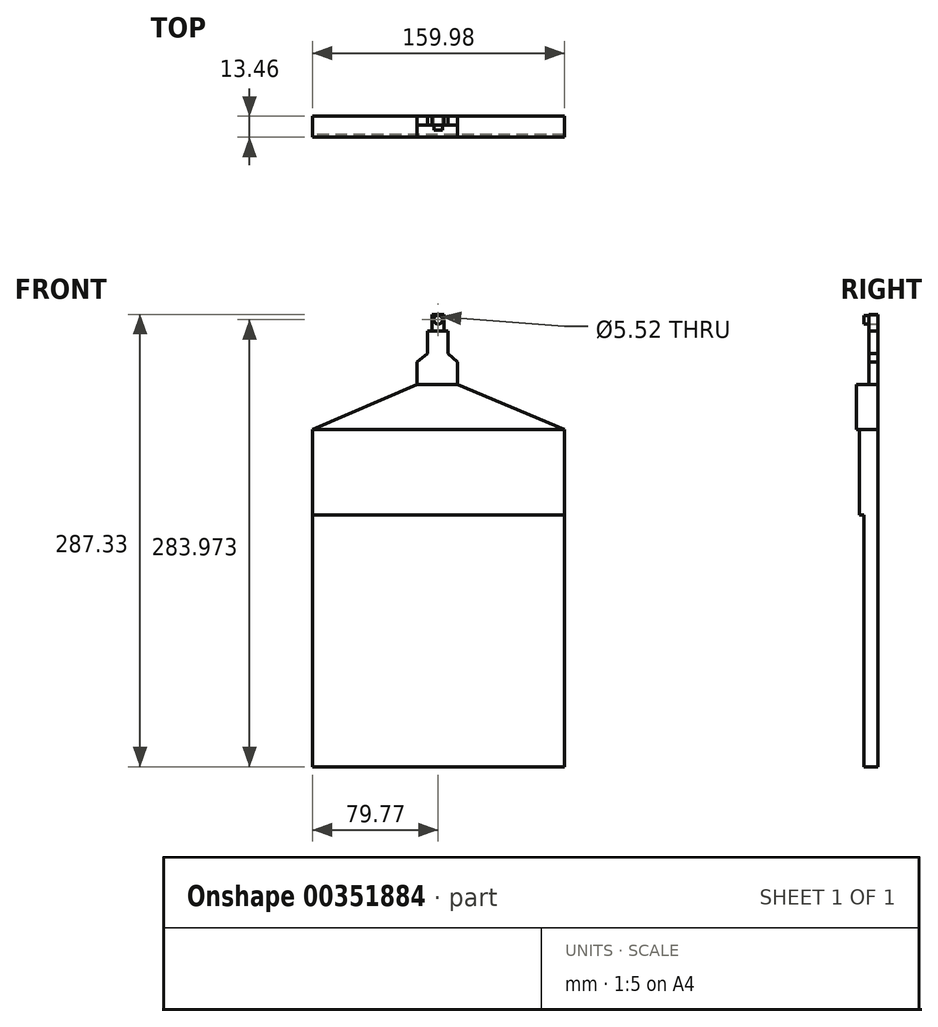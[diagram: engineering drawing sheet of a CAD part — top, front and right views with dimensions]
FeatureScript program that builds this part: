
annotation { "Feature Type Name" : "Feature", "Feature Type Description" : "" }
export const myFeature = defineFeature(function(context is Context, id is Id, definition is map)
    precondition{}
    {
        {
            var Q0;
            Q0=qCreatedBy(makeId("Front.planeOp"),FACE);
            var sketch = newSketch(context, id + "F0", { "sketchPlane" : qUnion([Q0])});
            skLineSegment(sketch, "E0", {"start": v(80.21, 80.05) * mm, "end": v(-79.77, 80.05) * mm});
            skLineSegment(sketch, "E1", {"start": v(-79.77, 80.05) * mm, "end": v(-79.77, 134.36) * mm});
            skLineSegment(sketch, "E2", {"start": v(80.21, 80.05) * mm, "end": v(80.21, 134.36) * mm});
            skLineSegment(sketch, "E3", {"start": v(-79.77, 134.36) * mm, "end": v(80.21, 134.36) * mm});
            skLineSegment(sketch, "E4", {"start": v(-79.77, 80.05) * mm, "end": v(-79.77, -79.93) * mm});
            skLineSegment(sketch, "E5", {"start": v(80.21, 80.05) * mm, "end": v(80.21, -79.93) * mm});
            skLineSegment(sketch, "E6", {"start": v(-79.77, -79.93) * mm, "end": v(80.21, -79.93) * mm});
            skLineSegment(sketch, "E7", {"start": v(-79.77, 134.36) * mm, "end": v(-13.44, 162.73) * mm});
            skLineSegment(sketch, "E8", {"start": v(80.21, 134.36) * mm, "end": v(12.4, 162.75) * mm});
            skLineSegment(sketch, "E9", {"start": v(-13.44, 162.73) * mm, "end": v(12.4, 162.75) * mm});
            skLineSegment(sketch, "E10", {"start": v(-13.44, 162.73) * mm, "end": v(-13.45, 177.03) * mm});
            skLineSegment(sketch, "E11", {"start": v(12.4, 162.75) * mm, "end": v(12.4, 177.03) * mm});
            skLineSegment(sketch, "E12", {"start": v(-13.45, 177.03) * mm, "end": v(12.4, 177.03) * mm});
            skLineSegment(sketch, "E13", {"start": v(12.4, 177.03) * mm, "end": v(0, 188.27) * mm});
            skLineSegment(sketch, "E14", {"start": v(-13.45, 177.03) * mm, "end": v(0, 188.27) * mm});
            skLineSegment(sketch, "E15", {"start": v(-6.73, 182.65) * mm, "end": v(-6.73, 196.87) * mm});
            skLineSegment(sketch, "E16", {"start": v(6.2, 182.65) * mm, "end": v(6.2, 196.87) * mm});
            skLineSegment(sketch, "E17", {"start": v(-6.73, 196.87) * mm, "end": v(6.2, 196.87) * mm});
            skLineSegment(sketch, "E18.bottom", {"start": v(-3.79, 192.76) * mm, "end": v(3.83, 192.76) * mm});
            skLineSegment(sketch, "E18.top", {"start": v(-3.79, 207.4) * mm, "end": v(3.83, 207.4) * mm});
            skLineSegment(sketch, "E18.left", {"start": v(-3.79, 192.76) * mm, "end": v(-3.79, 207.4) * mm});
            skLineSegment(sketch, "E18.right", {"start": v(3.83, 192.76) * mm, "end": v(3.83, 207.4) * mm});
            skCircle(sketch, "E19", {"center": v(0, 204.04) * mm, "radius": 2.76 * mm});
            skSolve(sketch);
        }
        {
            var Q0;
            Q0=makeQuery(id+"F0.imprint","IMPRINT",FACE,{"disambiguationData":[TD([[makeQuery(id+"F0.imprint","IMPRINT",EDGE,{"derivedFrom":sQuery(id+"F0.wireOp",EDGE,"E0")}),1.0]])]});
            extrude(context, id + "F1", {"entities" : qUnion([Q0]), "depth" : 8.9 * mm});
        }
        {
            var Q0;
            Q0=makeQuery(id+"F0.imprint","IMPRINT",FACE,{"disambiguationData":[TD([[makeQuery(id+"F0.imprint","IMPRINT",EDGE,{"derivedFrom":sQuery(id+"F0.wireOp",EDGE,"E0")}),-1.0]])]});
            extrude(context, id + "F2", {"entities" : qUnion([Q0]), "operationType" : NewBodyOperationType.ADD, "depth" : 11.68 * mm});
        }
        {
            var Q0;
            Q0=makeQuery(id+"F0.imprint","IMPRINT",FACE,{"disambiguationData":[TD([[makeQuery(id+"F0.imprint","IMPRINT",EDGE,{"derivedFrom":sQuery(id+"F0.wireOp",EDGE,"E3")}),1.0]])]});
            extrude(context, id + "F3", {"entities" : qUnion([Q0]), "operationType" : NewBodyOperationType.ADD, "depth" : 13.46 * mm});
        }
        {
            var Q0;
            Q0=makeQuery(id+"F0.imprint","IMPRINT",FACE,{"disambiguationData":[TD([[makeQuery(id+"F0.imprint","IMPRINT",EDGE,{"derivedFrom":sQuery(id+"F0.wireOp",EDGE,"E9")}),1.0]])]});
            extrude(context, id + "F4", {"entities" : qUnion([Q0]), "operationType" : NewBodyOperationType.ADD, "depth" : 5.6 * mm});
        }
        {
            var Q0;
            {var subQ1=sQuery(id+"F0.wireOp",EDGE,"E12");Q0=makeQuery(id+"F0.imprint","IMPRINT",FACE,{"disambiguationData":[TD([[makeQuery(id+"F0.imprint","IMPRINT",EDGE,{"derivedFrom":subQ1}),1.0]])]});}
            extrude(context, id + "F5", {"entities" : qUnion([Q0]), "operationType" : NewBodyOperationType.ADD, "depth" : 5.6 * mm});
        }
        {
            var Q0;
            {var subQ1=sQuery(id+"F0.wireOp",EDGE,"E15");Q0=makeQuery(id+"F0.imprint","IMPRINT",FACE,{"disambiguationData":[TD([[makeQuery(id+"F0.imprint","IMPRINT",EDGE,{"derivedFrom":subQ1}),-1.0]])]});}
            extrude(context, id + "F6", {"entities" : qUnion([Q0]), "operationType" : NewBodyOperationType.ADD, "depth" : 5.6 * mm});
        }
        {
            var Q0;
            {var subQ5=sQuery(id+"F0.wireOp",EDGE,"E18.bottom");Q0=makeQuery(id+"F0.imprint","IMPRINT",FACE,{"disambiguationData":[TD([[makeQuery(id+"F0.imprint","IMPRINT",EDGE,{"derivedFrom":subQ5}),1.0]])]});}
            extrude(context, id + "F7", {"entities" : qUnion([Q0]), "operationType" : NewBodyOperationType.ADD, "depth" : 5.6 * mm});
        }
        {
            var Q0;
            Q0=makeQuery(id+"F0.imprint","IMPRINT",FACE,{"disambiguationData":[TD([[makeQuery(id+"F0.imprint","IMPRINT",EDGE,{"derivedFrom":sQuery(id+"F0.wireOp",EDGE,"E19")}),1.0]])]});
            extrude(context, id + "F8", {"entities" : qUnion([Q0]), "depth" : 8.9 * mm});
        }
        {
            var Q0;
            {var subQ1=sQuery(id+"F0.wireOp",EDGE,"E18.top");Q0=makeQuery(id+"F0.imprint","IMPRINT",FACE,{"disambiguationData":[TD([[makeQuery(id+"F0.imprint","IMPRINT",EDGE,{"derivedFrom":subQ1}),-1.0]])]});}
            extrude(context, id + "F9", {"entities" : qUnion([Q0]), "depth" : 5.6 * mm});
        }
    });
